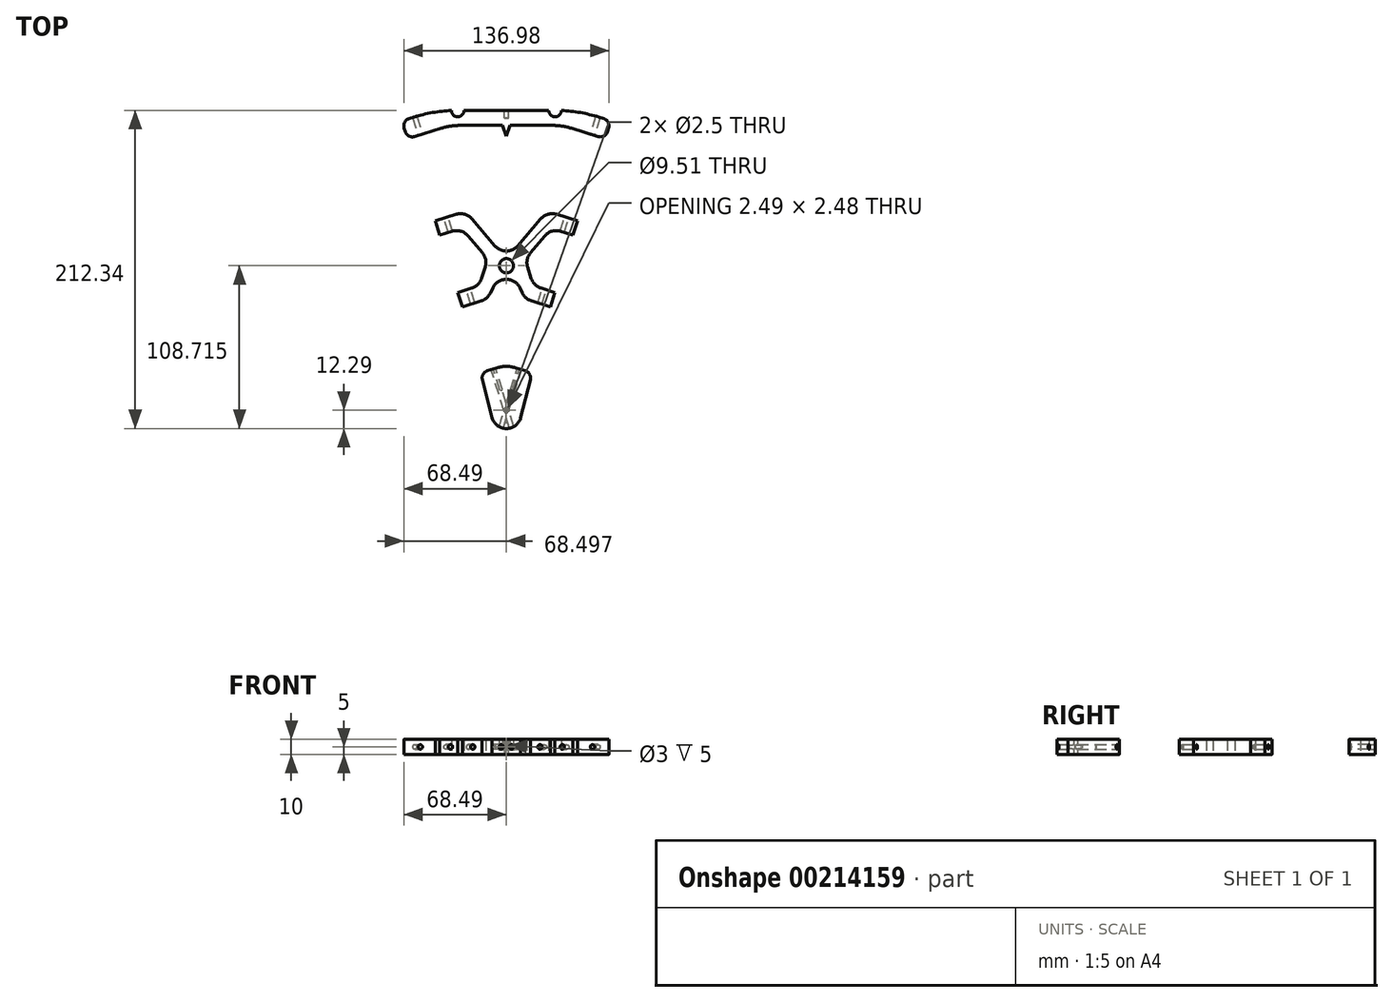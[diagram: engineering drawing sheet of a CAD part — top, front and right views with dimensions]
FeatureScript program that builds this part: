
annotation { "Feature Type Name" : "Feature", "Feature Type Description" : "" }
export const myFeature = defineFeature(function(context is Context, id is Id, definition is map)
    precondition{}
    {
        {
            var Q0;
            Q0=qCreatedBy(makeId("Top.planeOp"),FACE);
            var sketch = newSketch(context, id + "F0", { "sketchPlane" : qUnion([Q0])});
            skLineSegment(sketch, "E0.bottom", {"start": v(-47.5, 200.05) * mm, "end": v(-36.75, 200.05) * mm});
            skArc(sketch, "E1", {"start": v(-36.75, 200.05) * mm, "mid": v(-32.5, 195.8) * mm, "end": v(-28.25, 200.05) * mm});
            skArc(sketch, "E2", {"start": v(28.25, 200.05) * mm, "mid": v(32.5, 195.8) * mm, "end": v(36.75, 200.05) * mm});
            skLineSegment(sketch, "E3.trimOffspring", {"start": v(-28.25, 200.05) * mm, "end": v(28.25, 200.05) * mm});
            skLineSegment(sketch, "E4.trimOffspring", {"start": v(36.75, 200.05) * mm, "end": v(47.5, 200.05) * mm});
            skLineSegment(sketch, "E5", {"start": v(-47.5, 200.05) * mm, "end": v(-69.76, 193.1) * mm});
            skLineSegment(sketch, "E6", {"start": v(47.5, 200.05) * mm, "end": v(69.76, 193.1) * mm});
            skLineSegment(sketch, "E7", {"start": v(0, 0) * mm, "end": v(-62.5, 200.05) * mm, "construction": true});
            skLineSegment(sketch, "E8", {"start": v(0, 0) * mm, "end": v(62.5, 200.05) * mm, "construction": true});
            skLineSegment(sketch, "E9", {"start": v(-69.76, 193.1) * mm, "end": v(-66.02, 181.14) * mm});
            skLineSegment(sketch, "E10", {"start": v(-66.02, 181.14) * mm, "end": v(-37.5, 190.05) * mm});
            skLineSegment(sketch, "E11", {"start": v(66.02, 181.14) * mm, "end": v(69.76, 193.1) * mm});
            skLineSegment(sketch, "E12", {"start": v(0, 30.18) * mm, "end": v(-17.18, 24.81) * mm});
            skLineSegment(sketch, "E13", {"start": v(0, 30.18) * mm, "end": v(17.18, 24.81) * mm});
            skLineSegment(sketch, "E14", {"start": v(-17.18, 24.81) * mm, "end": v(-9.58, -5.16) * mm});
            skLineSegment(sketch, "E15", {"start": v(17.18, 24.81) * mm, "end": v(9.58, -5.16) * mm});
            skArc(sketch, "E16.trimOffspring", {"start": v(-9.58, -5.16) * mm, "mid": v(0, -12.29) * mm, "end": v(9.58, -5.16) * mm});
            skCircle(sketch, "E17", {"center": v(0, 0) * mm, "radius": 1.25 * mm});
            skLineSegment(sketch, "E18", {"start": v(47.5, 200.05) * mm, "end": v(144.63, 200.05) * mm, "construction": true});
            skLineSegment(sketch, "E19", {"start": v(37.5, 190.05) * mm, "end": v(2.5, 190.05) * mm});
            skLineSegment(sketch, "E20", {"start": v(66.02, 181.14) * mm, "end": v(37.5, 190.05) * mm});
            skLineSegment(sketch, "E21", {"start": v(-2.5, 190.05) * mm, "end": v(0, 183.05) * mm});
            skLineSegment(sketch, "E22", {"start": v(0, 183.05) * mm, "end": v(2.5, 190.05) * mm});
            skLineSegment(sketch, "E23.trimOffspring", {"start": v(-2.5, 190.05) * mm, "end": v(-37.5, 190.05) * mm});
            skLineSegment(sketch, "E24", {"start": v(33.51, 130.74) * mm, "end": v(47.47, 126.38) * mm});
            skLineSegment(sketch, "E25", {"start": v(47.47, 126.38) * mm, "end": v(44.49, 116.83) * mm});
            skLineSegment(sketch, "E26", {"start": v(44.49, 116.83) * mm, "end": v(36.24, 119.4) * mm});
            skLineSegment(sketch, "E27", {"start": v(25.65, 116.35) * mm, "end": v(16.08, 105.12) * mm});
            skLineSegment(sketch, "E28", {"start": v(14.15, 95.66) * mm, "end": v(16.53, 88.05) * mm});
            skLineSegment(sketch, "E29", {"start": v(23.1, 81.5) * mm, "end": v(32.4, 78.58) * mm});
            skLineSegment(sketch, "E30", {"start": v(32.4, 78.58) * mm, "end": v(29.43, 69.03) * mm});
            skLineSegment(sketch, "E31", {"start": v(29.43, 69.03) * mm, "end": v(16.7, 73.01) * mm});
            skLineSegment(sketch, "E32", {"start": v(10.63, 78.28) * mm, "end": v(9.04, 81.65) * mm});
            skLineSegment(sketch, "E33", {"start": v(22.92, 127.68) * mm, "end": v(7.61, 109.71) * mm});
            skLineSegment(sketch, "E34.MirrorCS", {"start": v(-44.49, 116.83) * mm, "end": v(-36.24, 119.4) * mm});
            skLineSegment(sketch, "E35.MirrorCS", {"start": v(-14.15, 95.66) * mm, "end": v(-16.53, 88.05) * mm});
            skLineSegment(sketch, "E36.MirrorCS", {"start": v(-32.4, 78.58) * mm, "end": v(-29.43, 69.03) * mm});
            skLineSegment(sketch, "E37.MirrorCS", {"start": v(-33.51, 130.74) * mm, "end": v(-47.47, 126.38) * mm});
            skLineSegment(sketch, "E38.MirrorCS", {"start": v(-47.47, 126.38) * mm, "end": v(-44.49, 116.83) * mm});
            skLineSegment(sketch, "E39.MirrorCS", {"start": v(-22.92, 127.68) * mm, "end": v(-7.61, 109.71) * mm});
            skLineSegment(sketch, "E40.MirrorCS", {"start": v(-29.43, 69.03) * mm, "end": v(-16.7, 73.01) * mm});
            skLineSegment(sketch, "E41.MirrorCS", {"start": v(-10.63, 78.28) * mm, "end": v(-9.04, 81.65) * mm});
            skLineSegment(sketch, "E42.MirrorCS", {"start": v(-23.1, 81.5) * mm, "end": v(-32.4, 78.58) * mm});
            skLineSegment(sketch, "E43.MirrorCS", {"start": v(-25.65, 116.35) * mm, "end": v(-16.08, 105.12) * mm});
            skPoint(sketch, "E44.visualSharp", {"position": v(27.2, 132.71) * mm});
            skArc(sketch, "E44.filletArc", {"start": v(33.51, 130.74) * mm, "mid": v(27.75, 130.8) * mm, "end": v(22.92, 127.68) * mm});
            skPoint(sketch, "E45.visualSharp", {"position": v(29.93, 121.38) * mm});
            skArc(sketch, "E45.filletArc", {"start": v(36.24, 119.4) * mm, "mid": v(30.49, 119.47) * mm, "end": v(25.65, 116.35) * mm});
            skPoint(sketch, "E46.visualSharp", {"position": v(18.09, 83.05) * mm});
            skArc(sketch, "E46.filletArc", {"start": v(16.53, 88.05) * mm, "mid": v(19, 83.96) * mm, "end": v(23.1, 81.5) * mm});
            skPoint(sketch, "E47.visualSharp", {"position": v(12.5, 74.32) * mm});
            skArc(sketch, "E47.filletArc", {"start": v(10.63, 78.28) * mm, "mid": v(13.1, 75.01) * mm, "end": v(16.7, 73.01) * mm});
            skPoint(sketch, "E48.visualSharp", {"position": v(-12.5, 74.32) * mm});
            skArc(sketch, "E48.filletArc", {"start": v(-16.7, 73.01) * mm, "mid": v(-13.1, 75.01) * mm, "end": v(-10.63, 78.28) * mm});
            skPoint(sketch, "E49.visualSharp", {"position": v(-18.09, 83.05) * mm});
            skArc(sketch, "E49.filletArc", {"start": v(-23.1, 81.5) * mm, "mid": v(-19, 83.96) * mm, "end": v(-16.53, 88.05) * mm});
            skPoint(sketch, "E50.visualSharp", {"position": v(-29.93, 121.38) * mm});
            skArc(sketch, "E50.filletArc", {"start": v(-25.65, 116.35) * mm, "mid": v(-30.49, 119.47) * mm, "end": v(-36.24, 119.4) * mm});
            skPoint(sketch, "E51.visualSharp", {"position": v(-27.2, 132.71) * mm});
            skArc(sketch, "E51.filletArc", {"start": v(-22.92, 127.68) * mm, "mid": v(-27.75, 130.8) * mm, "end": v(-33.51, 130.74) * mm});
            skPoint(sketch, "E52.visualSharp", {"position": v(0, 100.78) * mm});
            skArc(sketch, "E52.filletArc", {"start": v(-7.61, 109.71) * mm, "mid": v(0, 106.2) * mm, "end": v(7.61, 109.71) * mm});
            skPoint(sketch, "E53.visualSharp", {"position": v(-12.5, 100.92) * mm});
            skArc(sketch, "E53.filletArc", {"start": v(-14.15, 95.66) * mm, "mid": v(-13.9, 100.64) * mm, "end": v(-16.08, 105.12) * mm});
            skPoint(sketch, "E54.visualSharp", {"position": v(12.5, 100.92) * mm});
            skArc(sketch, "E54.filletArc", {"start": v(16.08, 105.12) * mm, "mid": v(13.9, 100.64) * mm, "end": v(14.15, 95.66) * mm});
            skArc(sketch, "E55.filletArc", {"start": v(9.04, 81.65) * mm, "mid": v(0, 87.38) * mm, "end": v(-9.04, 81.65) * mm});
            skCircle(sketch, "E56", {"center": v(0, 96.43) * mm, "radius": 4.75 * mm});
            skSolve(sketch);
        }
        {
            var Q0;
            Q0 = qSketchRegion(id + "F0", true);
            extrude(context, id + "F1", {"entities" : qUnion([Q0]), "depth" : 10 * mm});
        }
        {
            var Q0;
            Q0=makeQuery(id+"F1.opExtrude","SWEPT_FACE",FACE,{"disambiguationData":[OSD([sQuery(id+"F0.wireOp",EDGE,"E10")])]});
            var sketch = newSketch(context, id + "F2", { "sketchPlane" : qUnion([Q0])});
            skCircle(sketch, "E57", {"center": v(0, 5) * mm, "radius": 1.5 * mm});
            skSolve(sketch);
        }
        {
            var Q0;
            Q0=makeQuery(id+"F2.imprint","IMPRINT",FACE,{"disambiguationData":[TD([[makeQuery(id+"F2.imprint","IMPRINT",EDGE,{"derivedFrom":sQuery(id+"F2.wireOp",EDGE,"E57")}),1.0]])]});
            extrude(context, id + "F3", {"entities" : qUnion([Q0]), "operationType" : NewBodyOperationType.REMOVE, "oppositeDirection" : true, "depth" : 25 * mm});
        }
        {
            var Q0;
            Q0=makeQuery(id+"F1.opExtrude","SWEPT_FACE",FACE,{"disambiguationData":[OSD([sQuery(id+"F0.wireOp",EDGE,"E12")])]});
            var sketch = newSketch(context, id + "F4", { "sketchPlane" : qUnion([Q0])});
            skCircle(sketch, "E58", {"center": v(0, 5) * mm, "radius": 1.5 * mm});
            skSolve(sketch);
        }
        {
            var Q0;
            Q0=makeQuery(id+"F1.opExtrude","SWEPT_FACE",FACE,{"disambiguationData":[OSD([sQuery(id+"F0.wireOp",EDGE,"E13")])]});
            var sketch = newSketch(context, id + "F5", { "sketchPlane" : qUnion([Q0])});
            skCircle(sketch, "E59", {"center": v(0, 5) * mm, "radius": 1.5 * mm});
            skSolve(sketch);
        }
        {
            var Q0;
            Q0 = qSketchRegion(id + "F5", true);
            extrude(context, id + "F6", {"entities" : qUnion([Q0]), "operationType" : NewBodyOperationType.REMOVE, "oppositeDirection" : true, "depth" : 15 * mm});
        }
        {
            var Q0;
            Q0 = qSketchRegion(id + "F4", true);
            extrude(context, id + "F7", {"entities" : qUnion([Q0]), "operationType" : NewBodyOperationType.REMOVE, "oppositeDirection" : true, "depth" : 15 * mm});
        }
        {
            var Q0;
            Q0=makeQuery(id+"F1.opExtrude","SWEPT_FACE",FACE,{"disambiguationData":[OSD([sQuery(id+"F0.wireOp",EDGE,"E20")])]});
            var sketch = newSketch(context, id + "F8", { "sketchPlane" : qUnion([Q0])});
            skCircle(sketch, "E60", {"center": v(0, 5) * mm, "radius": 1.5 * mm});
            skSolve(sketch);
        }
        {
            var Q0;
            Q0 = qSketchRegion(id + "F8", true);
            extrude(context, id + "F9", {"entities" : qUnion([Q0]), "operationType" : NewBodyOperationType.REMOVE, "oppositeDirection" : true, "depth" : 25 * mm});
        }
        {
            var Q0;
            Q0=makeQuery(id+"F1.opExtrude","SWEPT_FACE",FACE,{"disambiguationData":[OSD([sQuery(id+"F0.wireOp",EDGE,"E3.trimOffspring")])]});
            var sketch = newSketch(context, id + "F10", { "sketchPlane" : qUnion([Q0])});
            skCircle(sketch, "E61", {"center": v(0, 5) * mm, "radius": 1.5 * mm});
            skSolve(sketch);
        }
        {
            var Q0;
            Q0 = qSketchRegion(id + "F10", true);
            extrude(context, id + "F11", {"entities" : qUnion([Q0]), "operationType" : NewBodyOperationType.REMOVE, "oppositeDirection" : true, "depth" : 5 * mm});
        }
        {
            var Q0;
            Q0=makeQuery(id+"F1.opExtrude","SWEPT_EDGE",EDGE,{"disambiguationData":[OSD([sQuery(id+"F0.wireOp",EDGE,"E5"),sQuery(id+"F0.wireOp",EDGE,"E9")])]});
            var Q1;
            Q1=makeQuery(id+"F1.opExtrude","SWEPT_EDGE",EDGE,{"disambiguationData":[OSD([sQuery(id+"F0.wireOp",EDGE,"E9"),sQuery(id+"F0.wireOp",EDGE,"E10")])]});
            var Q2;
            Q2=makeQuery(id+"F1.opExtrude","SWEPT_EDGE",EDGE,{"disambiguationData":[OSD([sQuery(id+"F0.wireOp",EDGE,"E6"),sQuery(id+"F0.wireOp",EDGE,"E11")])]});
            var Q3;
            Q3=makeQuery(id+"F1.opExtrude","SWEPT_EDGE",EDGE,{"disambiguationData":[OSD([sQuery(id+"F0.wireOp",EDGE,"E11"),sQuery(id+"F0.wireOp",EDGE,"E20")])]});
            var Q4;
            Q4=makeQuery(id+"F1.opExtrude","SWEPT_EDGE",EDGE,{"disambiguationData":[OSD([sQuery(id+"F0.wireOp",EDGE,"E13"),sQuery(id+"F0.wireOp",EDGE,"E15")])]});
            var Q5;
            Q5=makeQuery(id+"F1.opExtrude","SWEPT_EDGE",EDGE,{"disambiguationData":[OSD([sQuery(id+"F0.wireOp",EDGE,"E12"),sQuery(id+"F0.wireOp",EDGE,"E14")])]});
            fillet(context, id + "F12", {"entities" : qUnion([Q0, Q1, Q2, Q3, Q4, Q5]), "radius" : 5 * mm, "tangentPropagation" : true, "allowEdgeOverflow" : false});
        }
        {
            var Q0;
            Q0=makeQuery(id+"F1.opExtrude","SWEPT_EDGE",EDGE,{"disambiguationData":[OSD([sQuery(id+"F0.wireOp",EDGE,"E0.bottom"),sQuery(id+"F0.wireOp",EDGE,"E5")])]});
            var Q1;
            Q1=makeQuery(id+"F1.opExtrude","SWEPT_EDGE",EDGE,{"disambiguationData":[OSD([sQuery(id+"F0.wireOp",EDGE,"E4.trimOffspring"),sQuery(id+"F0.wireOp",EDGE,"E6")])]});
            fillet(context, id + "F13", {"entities" : qUnion([Q0, Q1]), "radius" : 100 * mm, "tangentPropagation" : true, "allowEdgeOverflow" : false});
        }
        {
            var Q0;
            Q0=makeQuery(id+"F1.opExtrude","SWEPT_EDGE",EDGE,{"disambiguationData":[OSD([sQuery(id+"F0.wireOp",EDGE,"E10"),sQuery(id+"F0.wireOp",EDGE,"E23.trimOffspring")])]});
            var Q1;
            Q1=makeQuery(id+"F1.opExtrude","SWEPT_EDGE",EDGE,{"disambiguationData":[OSD([sQuery(id+"F0.wireOp",EDGE,"E19"),sQuery(id+"F0.wireOp",EDGE,"E20")])]});
            fillet(context, id + "F14", {"entities" : qUnion([Q0, Q1]), "radius" : 40 * mm, "tangentPropagation" : true, "allowEdgeOverflow" : false});
        }
        {
            var Q0;
            Q0=makeQuery(id+"F1.opExtrude","SWEPT_EDGE",EDGE,{"disambiguationData":[OSD([sQuery(id+"F0.wireOp",EDGE,"E12"),sQuery(id+"F0.wireOp",EDGE,"E13")])]});
            fillet(context, id + "F15", {"entities" : qUnion([Q0]), "radius" : 20 * mm, "tangentPropagation" : true, "allowEdgeOverflow" : false});
        }
        {
            var Q0;
            Q0=makeQuery(id+"F1.opExtrude","SWEPT_FACE",FACE,{"disambiguationData":[OSD([sQuery(id+"F0.wireOp",EDGE,"E37.MirrorCS")])]});
            var sketch = newSketch(context, id + "F16", { "sketchPlane" : qUnion([Q0])});
            skCircle(sketch, "E62", {"center": v(0.12, 5) * mm, "radius": 1.5 * mm});
            skPoint(sketch, "E62.centerSnap0", {"position": v(7.62, 5) * mm});
            skSolve(sketch);
        }
        {
            var Q0;
            Q0=makeQuery(id+"F16.imprint","IMPRINT",FACE,{"disambiguationData":[TD([[makeQuery(id+"F16.imprint","IMPRINT",EDGE,{"derivedFrom":sQuery(id+"F16.wireOp",EDGE,"E62")}),1.0]])]});
            extrude(context, id + "F17", {"entities" : qUnion([Q0]), "operationType" : NewBodyOperationType.REMOVE, "endBound" : BoundingType.THROUGH_ALL, "oppositeDirection" : true, "depth" : 25 * mm});
        }
        {
            var Q0;
            Q0=makeQuery(id+"F1.opExtrude","SWEPT_FACE",FACE,{"disambiguationData":[OSD([sQuery(id+"F0.wireOp",EDGE,"E24")])]});
            var sketch = newSketch(context, id + "F18", { "sketchPlane" : qUnion([Q0])});
            skCircle(sketch, "E63", {"center": v(-0.12, 5) * mm, "radius": 1.5 * mm});
            skPoint(sketch, "E63.centerSnap0", {"position": v(-7.62, 5) * mm});
            skSolve(sketch);
        }
        {
            var Q0;
            Q0=makeQuery(id+"F18.imprint","IMPRINT",FACE,{"disambiguationData":[TD([[makeQuery(id+"F18.imprint","IMPRINT",EDGE,{"derivedFrom":sQuery(id+"F18.wireOp",EDGE,"E63")}),1.0]])]});
            extrude(context, id + "F19", {"entities" : qUnion([Q0]), "operationType" : NewBodyOperationType.REMOVE, "endBound" : BoundingType.THROUGH_ALL, "oppositeDirection" : true, "depth" : 25 * mm});
        }
    });
